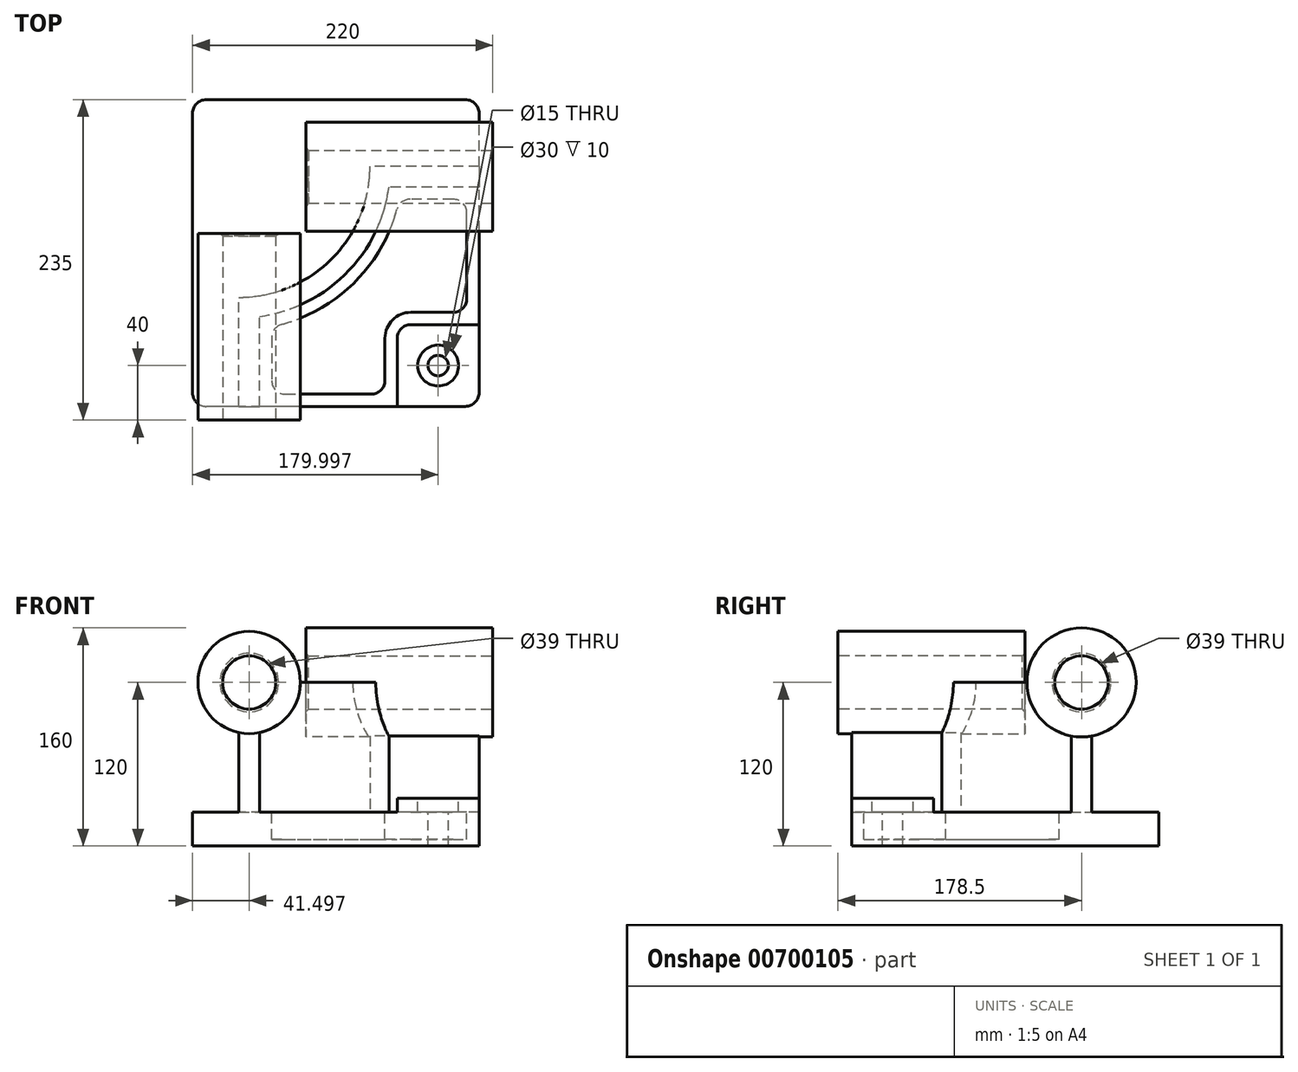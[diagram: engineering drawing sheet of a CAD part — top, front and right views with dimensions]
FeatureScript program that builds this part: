
annotation { "Feature Type Name" : "Feature", "Feature Type Description" : "" }
export const myFeature = defineFeature(function(context is Context, id is Id, definition is map)
    precondition{}
    {
        {
            var Q0;
            Q0=qCreatedBy(makeId("Top.planeOp"),FACE);
            var sketch = newSketch(context, id + "F0", { "sketchPlane" : qUnion([Q0])});
            skLineSegment(sketch, "E0.bottom", {"start": v(109.33, -112.5) * mm, "end": v(-100.67, -112.5) * mm});
            skLineSegment(sketch, "E0.top", {"start": v(109.33, 112.5) * mm, "end": v(-100.67, 112.5) * mm});
            skLineSegment(sketch, "E0.left", {"start": v(109.33, -112.5) * mm, "end": v(109.33, 112.5) * mm});
            skLineSegment(sketch, "E0.right", {"start": v(-100.67, -112.5) * mm, "end": v(-100.67, 112.5) * mm});
            skPoint(sketch, "E0.middle", {"position": v(4.33, 0) * mm});
            skSolve(sketch);
        }
        {
            var Q0;
            Q0=makeQuery(id+"F0.imprint","IMPRINT",FACE,{"disambiguationData":[TD([[makeQuery(id+"F0.imprint","IMPRINT",EDGE,{"derivedFrom":sQuery(id+"F0.wireOp",EDGE,"E0.bottom")}),-1.0]])]});
            extrude(context, id + "F1", {"entities" : qUnion([Q0]), "depth" : 25 * mm, "offsetDistance" : 25 * mm});
        }
        {
            var Q0;
            Q0=makeQuery(id+"F1.opExtrude","CAP_FACE",FACE,{"disambiguationData":[OSD([sQuery(id+"F0.wireOp",EDGE,"E0.bottom"),sQuery(id+"F0.wireOp",EDGE,"E0.top"),sQuery(id+"F0.wireOp",EDGE,"E0.left"),sQuery(id+"F0.wireOp",EDGE,"E0.right")])],"isStart":false});
            var sketch = newSketch(context, id + "F2", { "sketchPlane" : qUnion([Q0])});
            skLineSegment(sketch, "E1", {"start": v(-66.67, -112.5) * mm, "end": v(-66.67, -32.5) * mm});
            skLineSegment(sketch, "E2", {"start": v(109.33, 63.5) * mm, "end": v(29.33, 63.5) * mm});
            skArc(sketch, "E3", {"start": v(-66.67, -32.5) * mm, "mid": v(1.2, -4.38) * mm, "end": v(29.33, 63.5) * mm});
            skLineSegment(sketch, "E4", {"start": v(-66.67, 63.5) * mm, "end": v(-66.67, -32.5) * mm});
            skLineSegment(sketch, "E5", {"start": v(-66.67, 63.5) * mm, "end": v(29.33, 63.5) * mm});
            skLineSegment(sketch, "E6.0", {"start": v(-51.67, -112.5) * mm, "end": v(-51.67, -46.48) * mm});
            skArc(sketch, "E6.1", {"start": v(-51.67, -46.48) * mm, "mid": v(11.82, -14.99) * mm, "end": v(43.3, 48.5) * mm});
            skLineSegment(sketch, "E6.2", {"start": v(109.33, 48.5) * mm, "end": v(43.3, 48.5) * mm});
            skLineSegment(sketch, "E7.0", {"start": v(109.33, -112.5) * mm, "end": v(109.33, 112.5) * mm});
            skLineSegment(sketch, "E7.1", {"start": v(109.33, -112.5) * mm, "end": v(-100.67, -112.5) * mm});
            skSolve(sketch);
        }
        {
            var Q0;
            {var subQ2=sQuery(id+"F2.wireOp",EDGE,"E1");Q0=makeQuery(id+"F2.imprint","IMPRINT",FACE,{"disambiguationData":[TD([[makeQuery(id+"F2.imprint","IMPRINT",EDGE,{"derivedFrom":subQ2}),-1.0]])]});}
            extrude(context, id + "F3", {"entities" : qUnion([Q0]), "operationType" : NewBodyOperationType.ADD, "depth" : 95 * mm, "offsetDistance" : 25 * mm});
        }
        {
            var Q0;
            Q0=makeQuery(id+"F3.boolean.opBoolean","MERGE",FACE,{"derivedFrom":[makeQuery(id+"F1.opExtrude","SWEPT_FACE",FACE,{"disambiguationData":[OSD([sQuery(id+"F0.wireOp",EDGE,"E0.bottom")])]}),makeQuery(id+"F3.opExtrude","SWEPT_FACE",FACE,{"disambiguationData":[OSD([sQuery(id+"F2.wireOp",EDGE,"E7.1")])]})]});
            var sketch = newSketch(context, id + "F4", { "sketchPlane" : qUnion([Q0])});
            skCircle(sketch, "E8", {"center": v(-59.17, 120) * mm, "radius": 37.5 * mm});
            skSolve(sketch);
        }
        {
            var Q0;
            Q0 = qSketchRegion(id + "F4", true);
            extrude(context, id + "F5", {"entities" : qUnion([Q0]), "operationType" : NewBodyOperationType.ADD, "depth" : 10 * mm, "offsetDistance" : 25 * mm, "hasSecondDirection" : true, "secondDirectionOppositeDirection" : true, "secondDirectionDepth" : 127 * mm});
        }
        {
            var Q0;
            Q0=makeQuery(id+"F3.boolean.opBoolean","MERGE",FACE,{"derivedFrom":[makeQuery(id+"F1.opExtrude","SWEPT_FACE",FACE,{"disambiguationData":[OSD([sQuery(id+"F0.wireOp",EDGE,"E0.left")])]}),makeQuery(id+"F3.opExtrude","SWEPT_FACE",FACE,{"disambiguationData":[OSD([sQuery(id+"F2.wireOp",EDGE,"E7.0")])]})]});
            var sketch = newSketch(context, id + "F6", { "sketchPlane" : qUnion([Q0])});
            skCircle(sketch, "E9", {"center": v(56, 120) * mm, "radius": 40 * mm});
            skSolve(sketch);
        }
        {
            var Q0;
            Q0 = qSketchRegion(id + "F6", true);
            extrude(context, id + "F7", {"entities" : qUnion([Q0]), "operationType" : NewBodyOperationType.ADD, "depth" : 10 * mm, "offsetDistance" : 25 * mm, "hasSecondDirection" : true, "secondDirectionOppositeDirection" : true, "secondDirectionDepth" : (137 - 10) * mm});
        }
        {
            var Q0;
            {var subQ0=sQuery(id+"F0.wireOp",EDGE,"E0.left");var subQ1=sQuery(id+"F0.wireOp",EDGE,"E0.bottom");Q0=makeQuery(id+"F3.boolean.opBoolean","SPLIT",FACE,{"disambiguationData":[TD([makeQuery(id+"F3.opExtrude","SWEPT_FACE",FACE,{"disambiguationData":[OSD([sQuery(id+"F2.wireOp",EDGE,"E6.0")])]})])],"derivedFrom":makeQuery(id+"F1.opExtrude","CAP_FACE",FACE,{"disambiguationData":[OSD([subQ1,sQuery(id+"F0.wireOp",EDGE,"E0.top"),subQ0,sQuery(id+"F0.wireOp",EDGE,"E0.right")])],"isStart":false})});}
            var sketch = newSketch(context, id + "F8", { "sketchPlane" : qUnion([Q0])});
            skLineSegment(sketch, "E10.bottom", {"start": v(109.33, -112.5) * mm, "end": v(49.33, -112.5) * mm});
            skLineSegment(sketch, "E10.top", {"start": v(109.33, -52.5) * mm, "end": v(49.33, -52.5) * mm});
            skLineSegment(sketch, "E10.left", {"start": v(109.33, -112.5) * mm, "end": v(109.33, -52.5) * mm});
            skLineSegment(sketch, "E10.right", {"start": v(49.33, -112.5) * mm, "end": v(49.33, -52.5) * mm});
            skSolve(sketch);
        }
        {
            var Q0;
            Q0 = qSketchRegion(id + "F8", true);
            extrude(context, id + "F9", {"entities" : qUnion([Q0]), "operationType" : NewBodyOperationType.ADD, "depth" : 10 * mm, "offsetDistance" : 25 * mm});
        }
        {
            var Q0;
            Q0=makeQuery(id+"F9.opExtrude","SWEPT_EDGE",EDGE,{"disambiguationData":[OSD([sQuery(id+"F8.wireOp",EDGE,"E10.top"),sQuery(id+"F8.wireOp",EDGE,"E10.right")])]});
            fillet(context, id + "F10", {"entities" : qUnion([Q0]), "radius" : 10 * mm, "tangentPropagation" : true, "allowEdgeOverflow" : false});
        }
        {
            var Q0;
            {var subQ0=sQuery(id+"F0.wireOp",EDGE,"E0.left");var subQ1=sQuery(id+"F0.wireOp",EDGE,"E0.bottom");Q0=makeQuery(id+"F3.boolean.opBoolean","SPLIT",FACE,{"disambiguationData":[TD([makeQuery(id+"F3.opExtrude","SWEPT_FACE",FACE,{"disambiguationData":[OSD([sQuery(id+"F2.wireOp",EDGE,"E6.0")])]})])],"derivedFrom":makeQuery(id+"F1.opExtrude","CAP_FACE",FACE,{"disambiguationData":[OSD([subQ1,sQuery(id+"F0.wireOp",EDGE,"E0.top"),subQ0,sQuery(id+"F0.wireOp",EDGE,"E0.right")])],"isStart":false})});}
            var sketch = newSketch(context, id + "F11", { "sketchPlane" : qUnion([Q0])});
            skLineSegment(sketch, "E11.0", {"start": v(-42.67, -54.08) * mm, "end": v(-42.67, -103.5) * mm});
            skArc(sketch, "E11.1", {"start": v(50.9, 39.5) * mm, "mid": v(18.18, -21.35) * mm, "end": v(-42.67, -54.08) * mm});
            skLineSegment(sketch, "E11.2", {"start": v(-42.67, -103.5) * mm, "end": v(40.33, -103.5) * mm});
            skLineSegment(sketch, "E11.3", {"start": v(100.33, 39.5) * mm, "end": v(50.9, 39.5) * mm});
            skLineSegment(sketch, "E11.4", {"start": v(40.33, -103.5) * mm, "end": v(40.33, -62.5) * mm});
            skArc(sketch, "E11.5", {"start": v(40.33, -62.5) * mm, "mid": v(45.9, -49.06) * mm, "end": v(59.33, -43.5) * mm});
            skLineSegment(sketch, "E11.6", {"start": v(59.33, -43.5) * mm, "end": v(100.33, -43.5) * mm});
            skLineSegment(sketch, "E11.7", {"start": v(100.33, -43.5) * mm, "end": v(100.33, 39.5) * mm});
            skSolve(sketch);
        }
        {
            var Q0;
            Q0=makeQuery(id+"F11.imprint","IMPRINT",FACE,{"disambiguationData":[TD([[makeQuery(id+"F11.imprint","IMPRINT",EDGE,{"derivedFrom":sQuery(id+"F11.wireOp",EDGE,"E11.0")}),1.0]])]});
            extrude(context, id + "F12", {"entities" : qUnion([Q0]), "operationType" : NewBodyOperationType.REMOVE, "oppositeDirection" : true, "depth" : 20 * mm, "offsetDistance" : 25 * mm});
        }
        {
            var Q0;
            Q0=makeQuery(id+"F9.opExtrude","CAP_FACE",FACE,{"disambiguationData":[OSD([sQuery(id+"F8.wireOp",EDGE,"E10.bottom"),sQuery(id+"F8.wireOp",EDGE,"E10.top"),sQuery(id+"F8.wireOp",EDGE,"E10.left"),sQuery(id+"F8.wireOp",EDGE,"E10.right")])],"isStart":false});
            var sketch = newSketch(context, id + "F13", { "sketchPlane" : qUnion([Q0])});
            skCircle(sketch, "E12", {"center": v(79.33, -82.5) * mm, "radius": 15 * mm});
            skSolve(sketch);
        }
        {
            var Q0;
            Q0=sQuery(id+"F13.wireOp",VERTEX,"E12.center");
            var Q1;
            Q1=makeQuery(id+"F1.opExtrude","SWEPT_BODY",BODY,{"disambiguationData":[OSD([sQuery(id+"F0.wireOp",EDGE,"E0.bottom"),sQuery(id+"F0.wireOp",EDGE,"E0.top"),sQuery(id+"F0.wireOp",EDGE,"E0.left"),sQuery(id+"F0.wireOp",EDGE,"E0.right")])]});
            hole(context, id + "F14", {"style" : HoleStyle.C_BORE, "endStyle" : HoleEndStyle.THROUGH, "holeDiameter" : 15 * mm, "cBoreDiameter" : 30 * mm, "cBoreDepth" : 10 * mm, "majorDiameter" : 5 * mm, "isTappedThrough" : true, "tappedDepth" : 12 * mm, "tapClearance" : 3, "locations" : qUnion([Q0]), "scope" : qUnion([Q1])});
        }
        {
            var Q0;
            Q0=makeQuery(id+"F12.boolean.opBoolean","COPY",EDGE,{"derivedFrom":makeQuery(id+"F12.opExtrude","SWEPT_EDGE",EDGE,{"disambiguationData":[OSD([sQuery(id+"F11.wireOp",EDGE,"E11.0"),sQuery(id+"F11.wireOp",EDGE,"E11.1")])]})});
            var Q1;
            Q1=makeQuery(id+"F12.boolean.opBoolean","COPY",EDGE,{"derivedFrom":makeQuery(id+"F12.opExtrude","SWEPT_EDGE",EDGE,{"disambiguationData":[OSD([sQuery(id+"F11.wireOp",EDGE,"E11.1"),sQuery(id+"F11.wireOp",EDGE,"E11.3")])]})});
            var Q2;
            Q2=makeQuery(id+"F12.boolean.opBoolean","COPY",EDGE,{"derivedFrom":makeQuery(id+"F12.opExtrude","SWEPT_EDGE",EDGE,{"disambiguationData":[OSD([sQuery(id+"F11.wireOp",EDGE,"E11.0"),sQuery(id+"F11.wireOp",EDGE,"E11.2")])]})});
            var Q3;
            Q3=makeQuery(id+"F12.boolean.opBoolean","COPY",EDGE,{"derivedFrom":makeQuery(id+"F12.opExtrude","SWEPT_EDGE",EDGE,{"disambiguationData":[OSD([sQuery(id+"F11.wireOp",EDGE,"E11.3"),sQuery(id+"F11.wireOp",EDGE,"E11.7")])]})});
            var Q4;
            Q4=makeQuery(id+"F12.boolean.opBoolean","COPY",EDGE,{"derivedFrom":makeQuery(id+"F12.opExtrude","SWEPT_EDGE",EDGE,{"disambiguationData":[OSD([sQuery(id+"F11.wireOp",EDGE,"E11.6"),sQuery(id+"F11.wireOp",EDGE,"E11.7")])]})});
            var Q5;
            Q5=makeQuery(id+"F12.boolean.opBoolean","COPY",EDGE,{"derivedFrom":makeQuery(id+"F12.opExtrude","SWEPT_EDGE",EDGE,{"disambiguationData":[OSD([sQuery(id+"F11.wireOp",EDGE,"E11.2"),sQuery(id+"F11.wireOp",EDGE,"E11.4")])]})});
            fillet(context, id + "F15", {"entities" : qUnion([Q0, Q1, Q2, Q3, Q4, Q5]), "radius" : 10 * mm, "tangentPropagation" : true, "allowEdgeOverflow" : false});
        }
        {
            var Q0;
            Q0=makeQuery(id+"F5.opExtrude","CAP_FACE",FACE,{"disambiguationData":[OSD([sQuery(id+"F4.wireOp",EDGE,"E8")])],"isStart":false});
            var sketch = newSketch(context, id + "F16", { "sketchPlane" : qUnion([Q0])});
            skCircle(sketch, "E13", {"center": v(-59.17, 120) * mm, "radius": 19.5 * mm});
            skSolve(sketch);
        }
        {
            var Q0;
            Q0 = qSketchRegion(id + "F16", true);
            extrude(context, id + "F17", {"entities" : qUnion([Q0]), "operationType" : NewBodyOperationType.REMOVE, "endBound" : BoundingType.THROUGH_ALL, "oppositeDirection" : true, "depth" : 25 * mm, "offsetDistance" : 25 * mm});
        }
        {
            var Q0;
            Q0=makeQuery(id+"F7.opExtrude","CAP_FACE",FACE,{"disambiguationData":[OSD([sQuery(id+"F6.wireOp",EDGE,"E9")])],"isStart":false});
            var sketch = newSketch(context, id + "F18", { "sketchPlane" : qUnion([Q0])});
            skCircle(sketch, "E14", {"center": v(56, 120) * mm, "radius": 19.5 * mm});
            skSolve(sketch);
        }
        {
            var Q0;
            Q0 = qSketchRegion(id + "F18", true);
            extrude(context, id + "F19", {"entities" : qUnion([Q0]), "operationType" : NewBodyOperationType.REMOVE, "endBound" : BoundingType.THROUGH_ALL, "oppositeDirection" : true, "depth" : 25 * mm, "offsetDistance" : 25 * mm});
        }
        {
            var Q0;
            Q0=makeQuery(id+"F17.boolean.opBoolean","COPY",EDGE,{"derivedFrom":makeQuery(id+"F17.opExtrude","CAP_EDGE",EDGE,{"disambiguationData":[OSD([sQuery(id+"F16.wireOp",EDGE,"E13")])],"isStart":true})});
            var Q1;
            Q1=makeQuery(id+"F19.boolean.opBoolean","COPY",EDGE,{"derivedFrom":makeQuery(id+"F19.opExtrude","CAP_EDGE",EDGE,{"disambiguationData":[OSD([sQuery(id+"F18.wireOp",EDGE,"E14")])],"isStart":true})});
            var Q2;
            Q2=makeQuery(id+"F19.boolean.opBoolean","INTERSECT",EDGE,{"derivedFrom":[makeQuery(id+"F7.opExtrude","CAP_FACE",FACE,{"disambiguationData":[OSD([sQuery(id+"F6.wireOp",EDGE,"E9")])],"isStart":true}),makeQuery(id+"F19.opExtrude","SWEPT_FACE",FACE,{"disambiguationData":[OSD([sQuery(id+"F18.wireOp",EDGE,"E14")])]})]});
            var Q3;
            Q3=makeQuery(id+"F17.boolean.opBoolean","INTERSECT",EDGE,{"derivedFrom":[makeQuery(id+"F5.opExtrude","CAP_FACE",FACE,{"disambiguationData":[OSD([sQuery(id+"F4.wireOp",EDGE,"E8")])],"isStart":true}),makeQuery(id+"F17.opExtrude","SWEPT_FACE",FACE,{"disambiguationData":[OSD([sQuery(id+"F16.wireOp",EDGE,"E13")])]})]});
            chamfer(context, id + "F20", {"entities" : qUnion([Q0, Q1, Q2, Q3]), "width" : 2 * mm, "tangentPropagation" : true});
        }
        {
            var Q0;
            Q0=makeQuery(id+"F9.boolean.opBoolean","MERGE",EDGE,{"derivedFrom":[makeQuery(id+"F1.opExtrude","SWEPT_EDGE",EDGE,{"disambiguationData":[OSD([sQuery(id+"F0.wireOp",EDGE,"E0.bottom"),sQuery(id+"F0.wireOp",EDGE,"E0.left")])]}),makeQuery(id+"F9.opExtrude","SWEPT_EDGE",EDGE,{"disambiguationData":[OSD([sQuery(id+"F8.wireOp",EDGE,"E10.bottom"),sQuery(id+"F8.wireOp",EDGE,"E10.left")])]})]});
            var Q1;
            Q1=makeQuery(id+"F1.opExtrude","SWEPT_EDGE",EDGE,{"disambiguationData":[OSD([sQuery(id+"F0.wireOp",EDGE,"E0.top"),sQuery(id+"F0.wireOp",EDGE,"E0.left")])]});
            var Q2;
            Q2=makeQuery(id+"F1.opExtrude","SWEPT_EDGE",EDGE,{"disambiguationData":[OSD([sQuery(id+"F0.wireOp",EDGE,"E0.bottom"),sQuery(id+"F0.wireOp",EDGE,"E0.right")])]});
            var Q3;
            Q3=makeQuery(id+"F1.opExtrude","SWEPT_EDGE",EDGE,{"disambiguationData":[OSD([sQuery(id+"F0.wireOp",EDGE,"E0.top"),sQuery(id+"F0.wireOp",EDGE,"E0.right")])]});
            fillet(context, id + "F21", {"entities" : qUnion([Q0, Q1, Q2, Q3]), "radius" : 10 * mm, "tangentPropagation" : true, "allowEdgeOverflow" : false});
        }
    });
